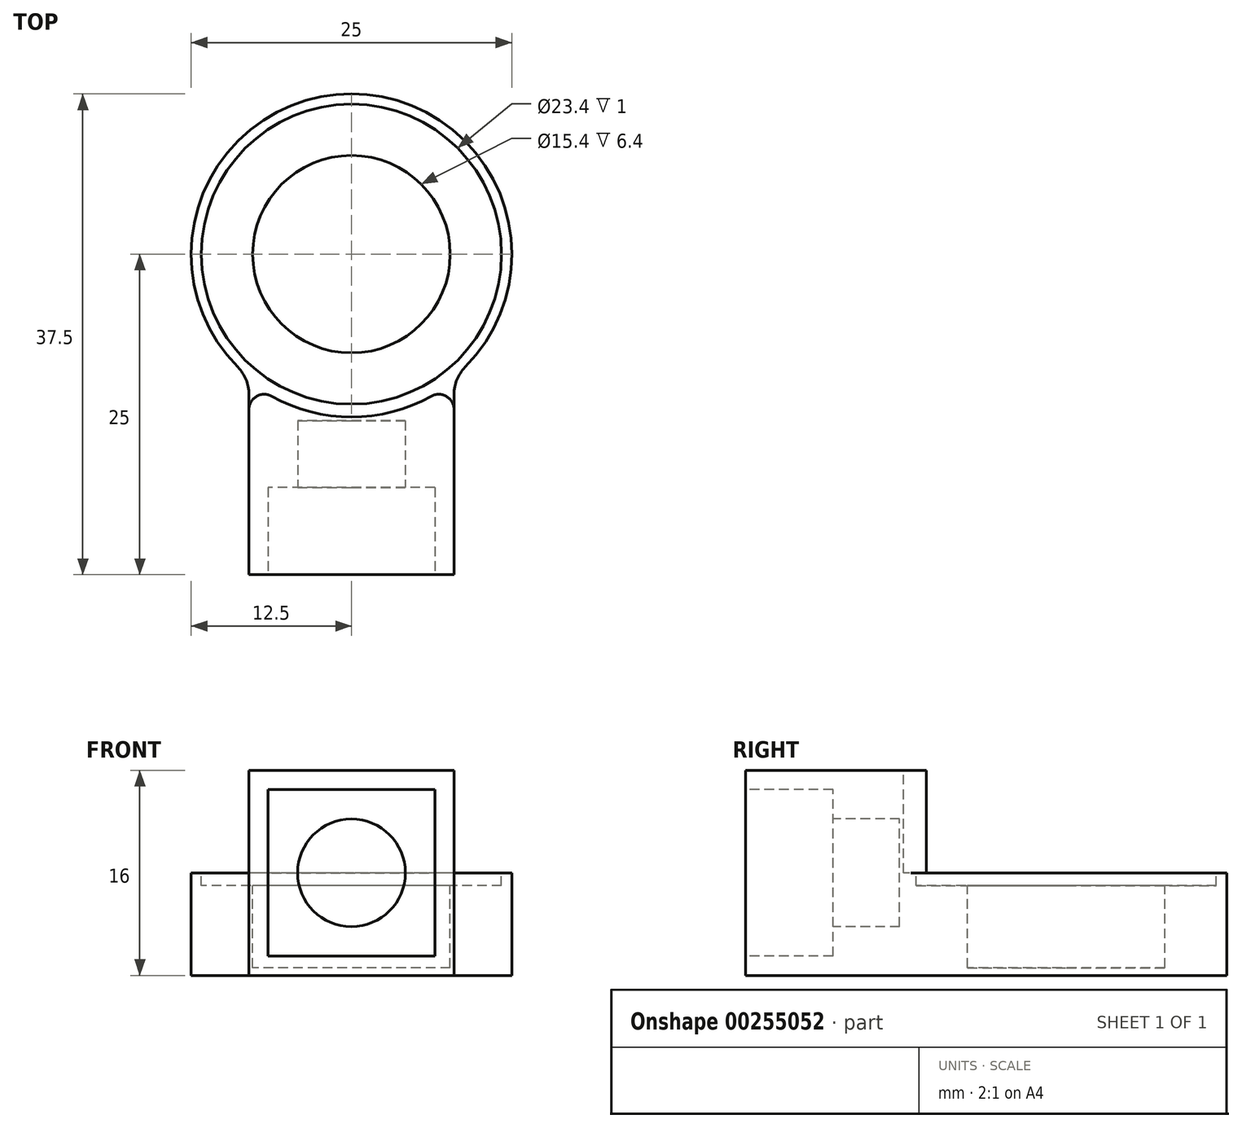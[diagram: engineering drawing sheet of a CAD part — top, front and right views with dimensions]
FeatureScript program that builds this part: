
annotation { "Feature Type Name" : "Feature", "Feature Type Description" : "" }
export const myFeature = defineFeature(function(context is Context, id is Id, definition is map)
    precondition{}
    {
        {
            var Q0;
            Q0=qCreatedBy(makeId("Top.planeOp"),FACE);
            var sketch = newSketch(context, id + "F0", { "sketchPlane" : qUnion([Q0])});
            skCircle(sketch, "E0", {"center": v(0, 0) * mm, "radius": 12.5 * mm});
            skLineSegment(sketch, "E1.bottom", {"start": v(8, -25) * mm, "end": v(-8, -25) * mm});
            skLineSegment(sketch, "E1.top", {"start": v(8, 0) * mm, "end": v(-8, 0) * mm});
            skLineSegment(sketch, "E1.left", {"start": v(8, -25) * mm, "end": v(8, 0) * mm});
            skLineSegment(sketch, "E1.right", {"start": v(-8, -25) * mm, "end": v(-8, 0) * mm});
            skPoint(sketch, "E1.middle", {"position": v(0, -12.5) * mm});
            skSolve(sketch);
        }
        {
            var Q0;
            Q0 = qSketchRegion(id + "F0", true);
            extrude(context, id + "F1", {"entities" : qUnion([Q0]), "depth" : 16 * mm});
        }
        {
            var Q0;
            Q0=makeQuery(id+"F1.opExtrude","CAP_FACE",FACE,{"disambiguationData":[OSD([sQuery(id+"F0.wireOp",EDGE,"E0"),sQuery(id+"F0.wireOp",EDGE,"E1.bottom"),sQuery(id+"F0.wireOp",EDGE,"E1.left"),sQuery(id+"F0.wireOp",EDGE,"E1.right")])],"isStart":false});
            var sketch = newSketch(context, id + "F2", { "sketchPlane" : qUnion([Q0])});
            skCircle(sketch, "E2", {"center": v(0, 0) * mm, "radius": 12.7 * mm});
            skSolve(sketch);
        }
        {
            var Q0;
            Q0 = qSketchRegion(id + "F2", true);
            extrude(context, id + "F3", {"entities" : qUnion([Q0]), "operationType" : NewBodyOperationType.REMOVE, "oppositeDirection" : true, "depth" : 8 * mm});
        }
        {
            var Q0;
            Q0=makeQuery(id+"F3.boolean.opBoolean","INTERSECT",EDGE,{"derivedFrom":[makeQuery(id+"F1.opExtrude","SWEPT_FACE",FACE,{"disambiguationData":[OSD([sQuery(id+"F0.wireOp",EDGE,"E1.right")])]}),makeQuery(id+"F3.opExtrude","SWEPT_FACE",FACE,{"disambiguationData":[OSD([sQuery(id+"F2.wireOp",EDGE,"E2")])]})]});
            var Q1;
            Q1=makeQuery(id+"F3.boolean.opBoolean","INTERSECT",EDGE,{"derivedFrom":[makeQuery(id+"F1.opExtrude","SWEPT_FACE",FACE,{"disambiguationData":[OSD([sQuery(id+"F0.wireOp",EDGE,"E1.left")])]}),makeQuery(id+"F3.opExtrude","SWEPT_FACE",FACE,{"disambiguationData":[OSD([sQuery(id+"F2.wireOp",EDGE,"E2")])]})]});
            fillet(context, id + "F4", {"entities" : qUnion([Q0, Q1]), "radius" : 1.2 * mm, "tangentPropagation" : true, "allowEdgeOverflow" : false});
        }
        {
            var Q0;
            Q0=makeQuery(id+"F1.opExtrude","SWEPT_EDGE",EDGE,{"disambiguationData":[OSD([sQuery(id+"F0.wireOp",EDGE,"E0"),sQuery(id+"F0.wireOp",EDGE,"E1.left")])]});
            var Q1;
            Q1=makeQuery(id+"F1.opExtrude","SWEPT_EDGE",EDGE,{"disambiguationData":[OSD([sQuery(id+"F0.wireOp",EDGE,"E0"),sQuery(id+"F0.wireOp",EDGE,"E1.right")])]});
            fillet(context, id + "F5", {"entities" : qUnion([Q0, Q1]), "radius" : 3 * mm, "tangentPropagation" : true, "allowEdgeOverflow" : false});
        }
        {
            var Q0;
            Q0=makeQuery(id+"F3.boolean.opBoolean","COPY",FACE,{"derivedFrom":makeQuery(id+"F3.opExtrude","CAP_FACE",FACE,{"disambiguationData":[OSD([sQuery(id+"F2.wireOp",EDGE,"E2")])],"isStart":false})});
            var sketch = newSketch(context, id + "F6", { "sketchPlane" : qUnion([Q0])});
            skCircle(sketch, "E3", {"center": v(0, 0) * mm, "radius": 11.7 * mm});
            skSolve(sketch);
        }
        {
            var Q0;
            Q0 = qSketchRegion(id + "F6", true);
            extrude(context, id + "F7", {"entities" : qUnion([Q0]), "operationType" : NewBodyOperationType.REMOVE, "oppositeDirection" : true, "depth" : 1 * mm});
        }
        {
            var Q0;
            Q0=makeQuery(id+"F7.boolean.opBoolean","COPY",FACE,{"derivedFrom":makeQuery(id+"F7.opExtrude","CAP_FACE",FACE,{"disambiguationData":[OSD([sQuery(id+"F6.wireOp",EDGE,"E3")])],"isStart":false})});
            var sketch = newSketch(context, id + "F8", { "sketchPlane" : qUnion([Q0])});
            skCircle(sketch, "E4", {"center": v(0, 0) * mm, "radius": 7.7 * mm});
            skSolve(sketch);
        }
        {
            var Q0;
            Q0 = qSketchRegion(id + "F8", true);
            extrude(context, id + "F9", {"entities" : qUnion([Q0]), "operationType" : NewBodyOperationType.REMOVE, "oppositeDirection" : true, "depth" : 6.4 * mm});
        }
        {
            var Q0;
            Q0=makeQuery(id+"F1.opExtrude","SWEPT_FACE",FACE,{"disambiguationData":[OSD([sQuery(id+"F0.wireOp",EDGE,"E1.bottom")])]});
            var sketch = newSketch(context, id + "F10", { "sketchPlane" : qUnion([Q0])});
            skLineSegment(sketch, "E5.bottom", {"start": v(6.5, 1.5) * mm, "end": v(-6.5, 1.5) * mm});
            skLineSegment(sketch, "E5.top", {"start": v(6.5, 14.5) * mm, "end": v(-6.5, 14.5) * mm});
            skLineSegment(sketch, "E5.left", {"start": v(6.5, 1.5) * mm, "end": v(6.5, 14.5) * mm});
            skLineSegment(sketch, "E5.right", {"start": v(-6.5, 1.5) * mm, "end": v(-6.5, 14.5) * mm});
            skPoint(sketch, "E5.middle", {"position": v(0, 8) * mm});
            skPoint(sketch, "E5.middle.positionSnap0", {"position": v(-8, 8) * mm});
            skPoint(sketch, "E5.centerSnap0", {"position": v(-8, 8) * mm});
            skSolve(sketch);
        }
        {
            var Q0;
            Q0 = qSketchRegion(id + "F10", true);
            extrude(context, id + "F11", {"entities" : qUnion([Q0]), "operationType" : NewBodyOperationType.REMOVE, "oppositeDirection" : true, "depth" : 6.8 * mm});
        }
        {
            var Q0;
            Q0=makeQuery(id+"F11.boolean.opBoolean","COPY",FACE,{"derivedFrom":makeQuery(id+"F11.opExtrude","CAP_FACE",FACE,{"disambiguationData":[OSD([sQuery(id+"F10.wireOp",EDGE,"E5.bottom"),sQuery(id+"F10.wireOp",EDGE,"E5.top"),sQuery(id+"F10.wireOp",EDGE,"E5.left"),sQuery(id+"F10.wireOp",EDGE,"E5.right")])],"isStart":false})});
            var sketch = newSketch(context, id + "F12", { "sketchPlane" : qUnion([Q0])});
            skCircle(sketch, "E6", {"center": v(0, 8) * mm, "radius": 4.2 * mm});
            skPoint(sketch, "E6.centerSnap0", {"position": v(6.5, 8) * mm});
            skPoint(sketch, "E6.centerSnap1", {"position": v(0, 1.5) * mm});
            skSolve(sketch);
        }
        {
            var Q0;
            Q0 = qSketchRegion(id + "F12", true);
            extrude(context, id + "F13", {"entities" : qUnion([Q0]), "operationType" : NewBodyOperationType.REMOVE, "oppositeDirection" : true, "depth" : 5.2 * mm});
        }
    });
